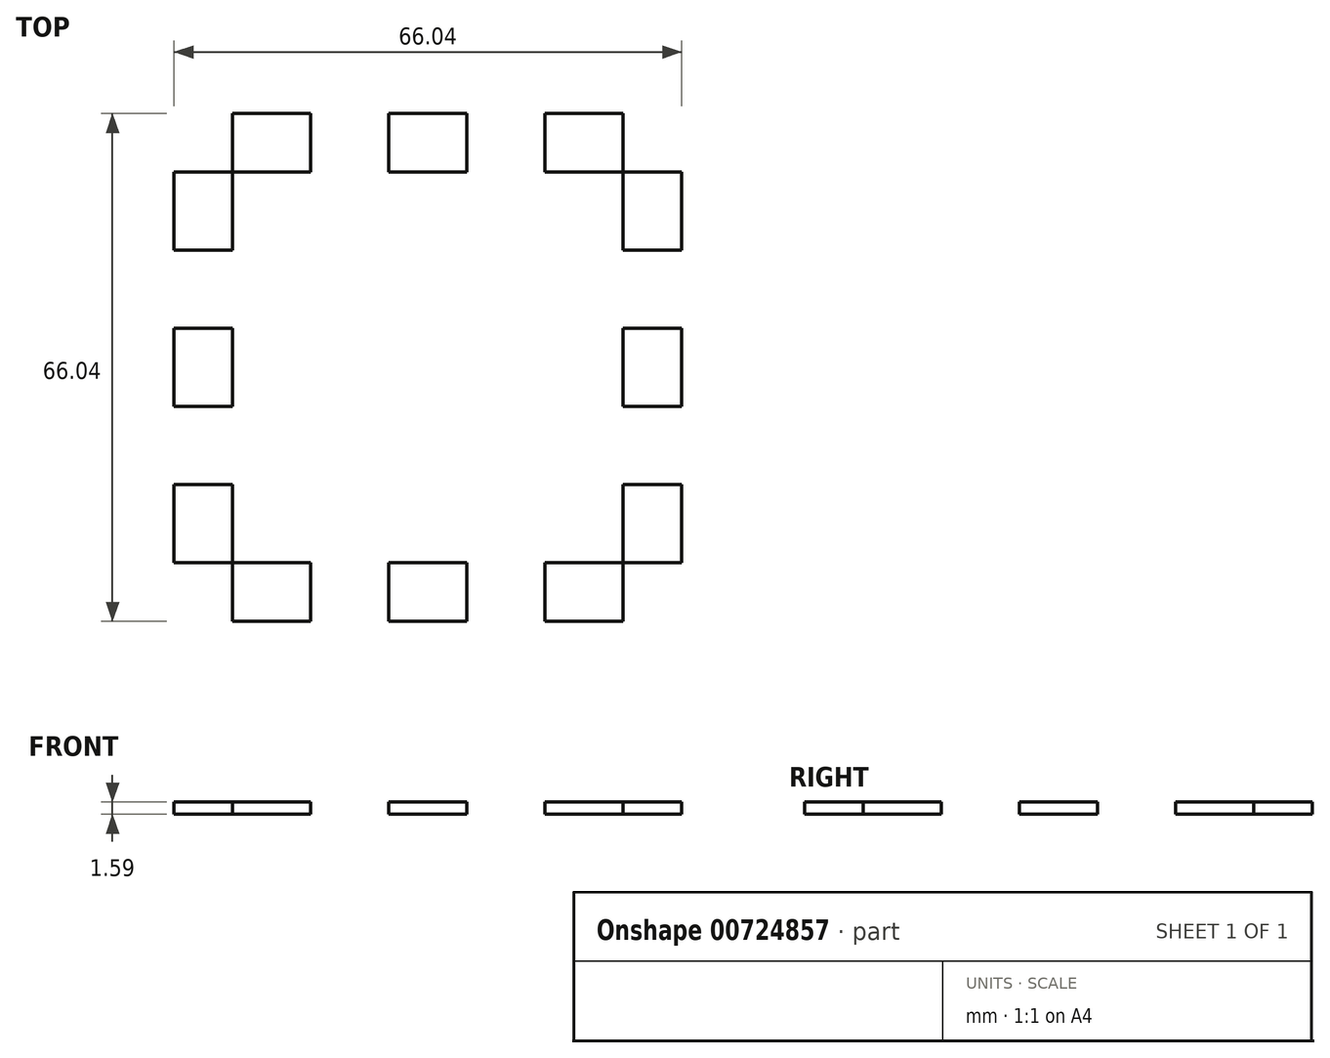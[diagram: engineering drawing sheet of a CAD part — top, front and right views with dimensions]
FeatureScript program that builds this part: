
annotation { "Feature Type Name" : "Feature", "Feature Type Description" : "" }
export const myFeature = defineFeature(function(context is Context, id is Id, definition is map)
    precondition{}
    {
        {
            var Q0;
            Q0=qCreatedBy(makeId("Top.planeOp"),FACE);
            var sketch = newSketch(context, id + "F0", { "sketchPlane" : qUnion([Q0])});
            skLineSegment(sketch, "E0.bottom", {"start": v(25.4, 25.4) * mm, "end": v(-25.4, 25.4) * mm});
            skLineSegment(sketch, "E0.top", {"start": v(25.4, -25.4) * mm, "end": v(-25.4, -25.4) * mm});
            skLineSegment(sketch, "E0.left", {"start": v(25.4, 25.4) * mm, "end": v(25.4, -25.4) * mm});
            skLineSegment(sketch, "E0.right", {"start": v(-25.4, 25.4) * mm, "end": v(-25.4, -25.4) * mm});
            skPoint(sketch, "E0.middle", {"position": v(0, 0) * mm});
            skLineSegment(sketch, "E1.bottom", {"start": v(25.4, -25.4) * mm, "end": v(33.02, -25.4) * mm});
            skLineSegment(sketch, "E1.top", {"start": v(25.4, -15.24) * mm, "end": v(33.02, -15.24) * mm});
            skLineSegment(sketch, "E1.left", {"start": v(25.4, -25.4) * mm, "end": v(25.4, -15.24) * mm});
            skLineSegment(sketch, "E1.right", {"start": v(33.02, -25.4) * mm, "end": v(33.02, -15.24) * mm});
            skLineSegment(sketch, "E2.bottom", {"start": v(25.4, 25.4) * mm, "end": v(33.02, 25.4) * mm});
            skLineSegment(sketch, "E2.top", {"start": v(25.4, 15.24) * mm, "end": v(33.02, 15.24) * mm});
            skLineSegment(sketch, "E2.left", {"start": v(25.4, 25.4) * mm, "end": v(25.4, 15.24) * mm});
            skLineSegment(sketch, "E2.right", {"start": v(33.02, 25.4) * mm, "end": v(33.02, 15.24) * mm});
            skLineSegment(sketch, "E3", {"start": v(25.4, -15.24) * mm, "end": v(25.4, -5.08) * mm});
            skLineSegment(sketch, "E4.bottom", {"start": v(25.4, -5.08) * mm, "end": v(33.02, -5.08) * mm});
            skLineSegment(sketch, "E4.top", {"start": v(25.4, 5.08) * mm, "end": v(33.02, 5.08) * mm});
            skLineSegment(sketch, "E4.left", {"start": v(25.4, -5.08) * mm, "end": v(25.4, 5.08) * mm});
            skLineSegment(sketch, "E4.right", {"start": v(33.02, -5.08) * mm, "end": v(33.02, 5.08) * mm});
            skLineSegment(sketch, "E5", {"start": v(25.4, 5.08) * mm, "end": v(25.4, 15.24) * mm});
            skLineSegment(sketch, "E6.bottom", {"start": v(25.4, 25.4) * mm, "end": v(25.4, 33.02) * mm});
            skLineSegment(sketch, "E6.top", {"start": v(15.24, 25.4) * mm, "end": v(15.24, 33.02) * mm});
            skLineSegment(sketch, "E6.right", {"start": v(25.4, 33.02) * mm, "end": v(15.24, 33.02) * mm});
            skLineSegment(sketch, "E7.bottom", {"start": v(-25.4, 25.4) * mm, "end": v(-25.4, 33.02) * mm});
            skLineSegment(sketch, "E7.top", {"start": v(-15.24, 25.4) * mm, "end": v(-15.24, 33.02) * mm});
            skLineSegment(sketch, "E7.right", {"start": v(-25.4, 33.02) * mm, "end": v(-15.24, 33.02) * mm});
            skLineSegment(sketch, "E8.bottom", {"start": v(5.08, 25.4) * mm, "end": v(5.08, 33.02) * mm});
            skLineSegment(sketch, "E8.top", {"start": v(-5.08, 25.4) * mm, "end": v(-5.08, 33.02) * mm});
            skLineSegment(sketch, "E8.right", {"start": v(5.08, 33.02) * mm, "end": v(-5.08, 33.02) * mm});
            skLineSegment(sketch, "E9.bottom", {"start": v(-25.4, 25.4) * mm, "end": v(-33.02, 25.4) * mm});
            skLineSegment(sketch, "E9.top", {"start": v(-25.4, 15.24) * mm, "end": v(-33.02, 15.24) * mm});
            skLineSegment(sketch, "E9.right", {"start": v(-33.02, 25.4) * mm, "end": v(-33.02, 15.24) * mm});
            skLineSegment(sketch, "E10.bottom", {"start": v(-25.4, -25.4) * mm, "end": v(-33.02, -25.4) * mm});
            skLineSegment(sketch, "E10.top", {"start": v(-25.4, -15.24) * mm, "end": v(-33.02, -15.24) * mm});
            skLineSegment(sketch, "E10.right", {"start": v(-33.02, -25.4) * mm, "end": v(-33.02, -15.24) * mm});
            skLineSegment(sketch, "E11.bottom", {"start": v(-25.4, 5.08) * mm, "end": v(-33.02, 5.08) * mm});
            skLineSegment(sketch, "E11.top", {"start": v(-25.4, -5.08) * mm, "end": v(-33.02, -5.08) * mm});
            skLineSegment(sketch, "E11.right", {"start": v(-33.02, 5.08) * mm, "end": v(-33.02, -5.08) * mm});
            skLineSegment(sketch, "E12.bottom", {"start": v(-25.4, -25.4) * mm, "end": v(-25.4, -33.02) * mm});
            skLineSegment(sketch, "E12.top", {"start": v(-15.24, -25.4) * mm, "end": v(-15.24, -33.02) * mm});
            skLineSegment(sketch, "E12.right", {"start": v(-25.4, -33.02) * mm, "end": v(-15.24, -33.02) * mm});
            skLineSegment(sketch, "E13.bottom", {"start": v(25.4, -25.4) * mm, "end": v(25.4, -33.02) * mm});
            skLineSegment(sketch, "E13.top", {"start": v(15.24, -25.4) * mm, "end": v(15.24, -33.02) * mm});
            skLineSegment(sketch, "E13.right", {"start": v(25.4, -33.02) * mm, "end": v(15.24, -33.02) * mm});
            skLineSegment(sketch, "E14.bottom", {"start": v(-5.08, -25.4) * mm, "end": v(-5.08, -33.02) * mm});
            skLineSegment(sketch, "E14.top", {"start": v(5.08, -25.4) * mm, "end": v(5.08, -33.02) * mm});
            skLineSegment(sketch, "E14.right", {"start": v(-5.08, -33.02) * mm, "end": v(5.08, -33.02) * mm});
            skSolve(sketch);
        }
        {
            var Q0;
            Q0=makeQuery(id+"F0.imprint","IMPRINT",FACE,{"disambiguationData":[TD([[makeQuery(id+"F0.imprint","IMPRINT",EDGE,{"derivedFrom":sQuery(id+"F0.wireOp",EDGE,"E1.bottom")}),1.0]])]});
            var Q1;
            {var subQ0=sQuery(id+"F0.wireOp",EDGE,"E13.bottom");Q1=makeQuery(id+"F0.imprint","IMPRINT",FACE,{"disambiguationData":[TD([[makeQuery(id+"F0.imprint","IMPRINT",EDGE,{"derivedFrom":subQ0}),-1.0]])]});}
            var Q2;
            {var subQ0=sQuery(id+"F0.wireOp",EDGE,"E14.bottom");Q2=makeQuery(id+"F0.imprint","IMPRINT",FACE,{"disambiguationData":[TD([[makeQuery(id+"F0.imprint","IMPRINT",EDGE,{"derivedFrom":subQ0}),1.0]])]});}
            var Q3;
            {var subQ0=sQuery(id+"F0.wireOp",EDGE,"E12.bottom");Q3=makeQuery(id+"F0.imprint","IMPRINT",FACE,{"disambiguationData":[TD([[makeQuery(id+"F0.imprint","IMPRINT",EDGE,{"derivedFrom":subQ0}),1.0]])]});}
            var Q4;
            {var subQ0=sQuery(id+"F0.wireOp",EDGE,"E10.bottom");Q4=makeQuery(id+"F0.imprint","IMPRINT",FACE,{"disambiguationData":[TD([[makeQuery(id+"F0.imprint","IMPRINT",EDGE,{"derivedFrom":subQ0}),-1.0]])]});}
            var Q5;
            {var subQ0=sQuery(id+"F0.wireOp",EDGE,"E11.bottom");Q5=makeQuery(id+"F0.imprint","IMPRINT",FACE,{"disambiguationData":[TD([[makeQuery(id+"F0.imprint","IMPRINT",EDGE,{"derivedFrom":subQ0}),1.0]])]});}
            var Q6;
            {var subQ0=sQuery(id+"F0.wireOp",EDGE,"E9.bottom");Q6=makeQuery(id+"F0.imprint","IMPRINT",FACE,{"disambiguationData":[TD([[makeQuery(id+"F0.imprint","IMPRINT",EDGE,{"derivedFrom":subQ0}),1.0]])]});}
            var Q7;
            {var subQ0=sQuery(id+"F0.wireOp",EDGE,"E7.bottom");Q7=makeQuery(id+"F0.imprint","IMPRINT",FACE,{"disambiguationData":[TD([[makeQuery(id+"F0.imprint","IMPRINT",EDGE,{"derivedFrom":subQ0}),-1.0]])]});}
            var Q8;
            {var subQ0=sQuery(id+"F0.wireOp",EDGE,"E8.bottom");Q8=makeQuery(id+"F0.imprint","IMPRINT",FACE,{"disambiguationData":[TD([[makeQuery(id+"F0.imprint","IMPRINT",EDGE,{"derivedFrom":subQ0}),1.0]])]});}
            var Q9;
            {var subQ0=sQuery(id+"F0.wireOp",EDGE,"E6.bottom");Q9=makeQuery(id+"F0.imprint","IMPRINT",FACE,{"disambiguationData":[TD([[makeQuery(id+"F0.imprint","IMPRINT",EDGE,{"derivedFrom":subQ0}),1.0]])]});}
            var Q10;
            Q10=makeQuery(id+"F0.imprint","IMPRINT",FACE,{"disambiguationData":[TD([[makeQuery(id+"F0.imprint","IMPRINT",EDGE,{"derivedFrom":sQuery(id+"F0.wireOp",EDGE,"E2.bottom")}),-1.0]])]});
            var Q11;
            {var subQ7=sQuery(id+"F0.wireOp",EDGE,"E1.left");Q11=makeQuery(id+"F0.imprint","IMPRINT",FACE,{"disambiguationData":[TD([[makeQuery(id+"F0.imprint","IMPRINT",EDGE,{"derivedFrom":subQ7}),1.0]])]});}
            var Q12;
            Q12=makeQuery(id+"F0.imprint","IMPRINT",FACE,{"disambiguationData":[TD([[makeQuery(id+"F0.imprint","IMPRINT",EDGE,{"derivedFrom":sQuery(id+"F0.wireOp",EDGE,"E4.bottom")}),1.0]])]});
            extrude(context, id + "F1", {"entities" : qUnion([Q0, Q1, Q2, Q3, Q4, Q5, Q6, Q7, Q8, Q9, Q10, Q11, Q12]), "depth" : 1.59 * mm, "offsetDistance" : 25.4 * mm});
        }
    });
